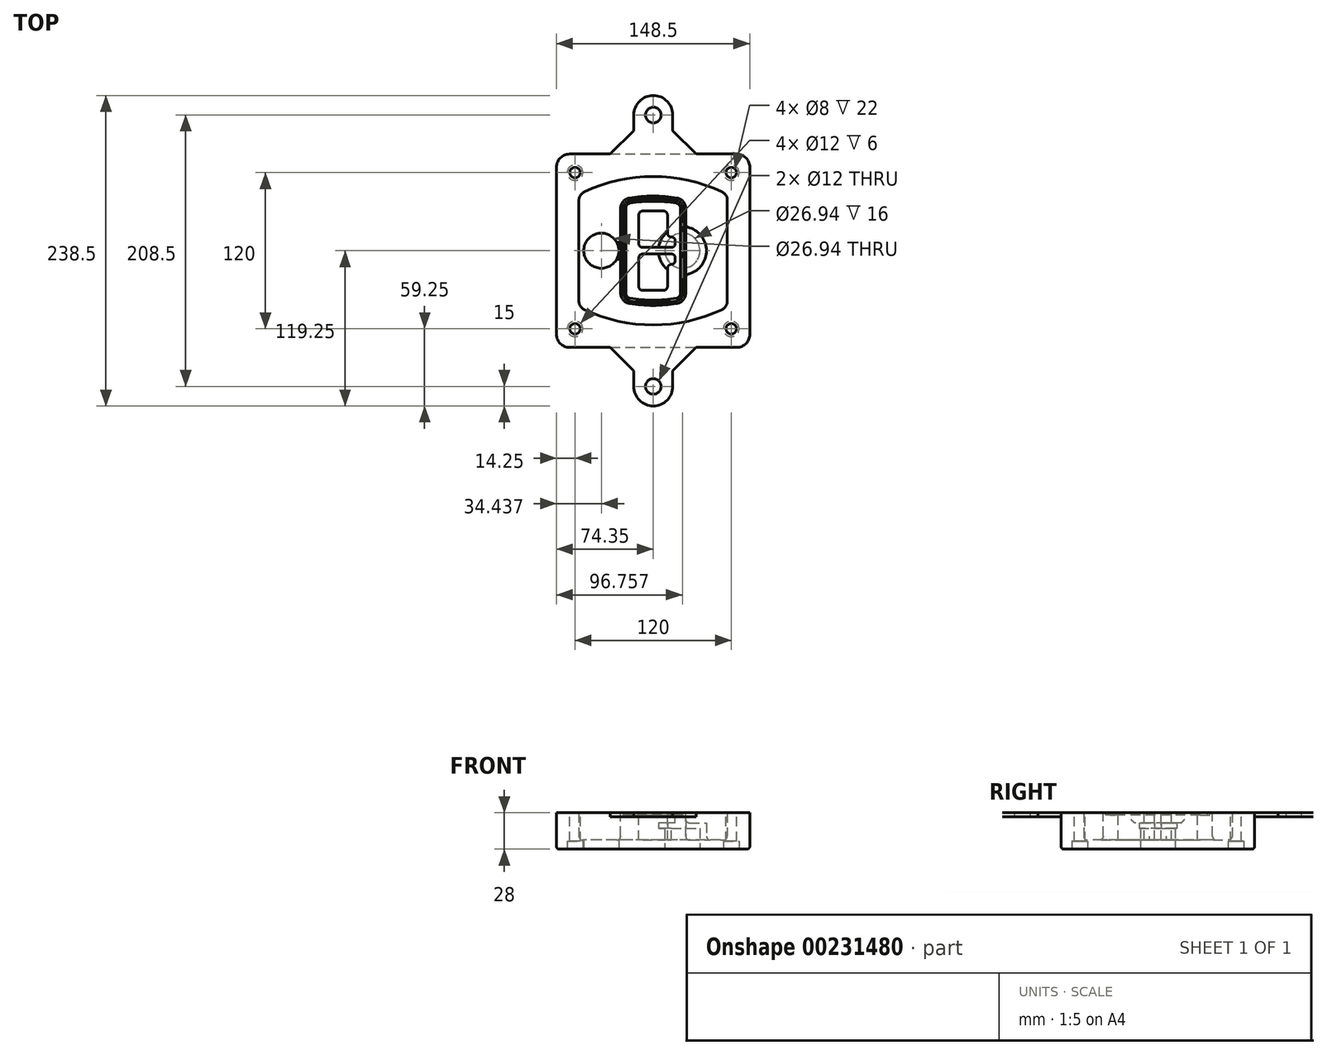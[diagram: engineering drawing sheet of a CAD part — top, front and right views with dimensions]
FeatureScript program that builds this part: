
annotation { "Feature Type Name" : "Feature", "Feature Type Description" : "" }
export const myFeature = defineFeature(function(context is Context, id is Id, definition is map)
    precondition{}
    {
        {
            var Q0;
            Q0=qCreatedBy(makeId("Top.planeOp"),FACE);
            var sketch = newSketch(context, id + "F0", { "sketchPlane" : qUnion([Q0])});
            skPoint(sketch, "E0.rect.middle", {"position": v(0, 0) * mm});
            skLineSegment(sketch, "E1.bottom", {"start": v(-64.25, -74.25) * mm, "end": v(64.25, -74.25) * mm});
            skLineSegment(sketch, "E1.top", {"start": v(-64.25, 74.25) * mm, "end": v(64.25, 74.25) * mm});
            skLineSegment(sketch, "E1.left", {"start": v(-74.25, -64.25) * mm, "end": v(-74.25, 64.25) * mm});
            skLineSegment(sketch, "E1.right", {"start": v(74.25, -64.25) * mm, "end": v(74.25, 64.25) * mm});
            skLineSegment(sketch, "E2", {"start": v(-74.25, 74.25) * mm, "end": v(74.25, -74.25) * mm, "construction": true});
            skLineSegment(sketch, "E3", {"start": v(74.25, 74.25) * mm, "end": v(-74.25, -74.25) * mm, "construction": true});
            skCircle(sketch, "E4", {"center": v(-60, 60) * mm, "radius": 4 * mm});
            skCircle(sketch, "E5", {"center": v(60, 60) * mm, "radius": 4 * mm});
            skCircle(sketch, "E6", {"center": v(60, -60) * mm, "radius": 4 * mm});
            skCircle(sketch, "E7", {"center": v(-60, -60) * mm, "radius": 4 * mm});
            skLineSegment(sketch, "E8", {"start": v(-60, 60) * mm, "end": v(60, 60) * mm, "construction": true});
            skLineSegment(sketch, "E9", {"start": v(60, 60) * mm, "end": v(60, -60) * mm, "construction": true});
            skLineSegment(sketch, "E10", {"start": v(60, -60) * mm, "end": v(-60, -60) * mm, "construction": true});
            skLineSegment(sketch, "E11", {"start": v(-60, -60) * mm, "end": v(-60, 60) * mm, "construction": true});
            skLineSegment(sketch, "E12", {"start": v(-60, 38.83) * mm, "end": v(-60, -38.83) * mm});
            skLineSegment(sketch, "E13", {"start": v(60, 38.83) * mm, "end": v(60, -38.83) * mm});
            skArc(sketch, "E14", {"start": v(54.26, 47.88) * mm, "mid": v(0, 60) * mm, "end": v(-54.26, 47.88) * mm});
            skArc(sketch, "E15", {"start": v(-54.26, -47.88) * mm, "mid": v(0, -60) * mm, "end": v(54.26, -47.88) * mm});
            skLineSegment(sketch, "E16", {"start": v(-60, 0) * mm, "end": v(60, 0) * mm, "construction": true});
            skPoint(sketch, "E17.visualSharp", {"position": v(-60, -45) * mm});
            skArc(sketch, "E17.filletArc", {"start": v(-60, -38.83) * mm, "mid": v(-58.44, -44.2) * mm, "end": v(-54.26, -47.88) * mm});
            skPoint(sketch, "E18.visualSharp", {"position": v(-60, 45) * mm});
            skArc(sketch, "E18.filletArc", {"start": v(-54.26, 47.88) * mm, "mid": v(-58.44, 44.2) * mm, "end": v(-60, 38.83) * mm});
            skPoint(sketch, "E19.visualSharp", {"position": v(60, 45) * mm});
            skArc(sketch, "E19.filletArc", {"start": v(60, 38.83) * mm, "mid": v(58.44, 44.2) * mm, "end": v(54.26, 47.88) * mm});
            skPoint(sketch, "E20.visualSharp", {"position": v(60, -45) * mm});
            skArc(sketch, "E20.filletArc", {"start": v(54.26, -47.88) * mm, "mid": v(58.44, -44.2) * mm, "end": v(60, -38.83) * mm});
            skPoint(sketch, "E21.visualSharp", {"position": v(-74.25, 74.25) * mm});
            skArc(sketch, "E21.filletArc", {"start": v(-64.25, 74.25) * mm, "mid": v(-71.32, 71.32) * mm, "end": v(-74.25, 64.25) * mm});
            skPoint(sketch, "E22.visualSharp", {"position": v(74.25, 74.25) * mm});
            skArc(sketch, "E22.filletArc", {"start": v(74.25, 64.25) * mm, "mid": v(71.32, 71.32) * mm, "end": v(64.25, 74.25) * mm});
            skPoint(sketch, "E23.visualSharp", {"position": v(74.25, -74.25) * mm});
            skArc(sketch, "E23.filletArc", {"start": v(64.25, -74.25) * mm, "mid": v(71.32, -71.32) * mm, "end": v(74.25, -64.25) * mm});
            skPoint(sketch, "E24.visualSharp", {"position": v(-74.25, -74.25) * mm});
            skArc(sketch, "E24.filletArc", {"start": v(-74.25, -64.25) * mm, "mid": v(-71.32, -71.32) * mm, "end": v(-64.25, -74.25) * mm});
            skArc(sketch, "E25.0", {"start": v(57, 38.83) * mm, "mid": v(55.9, 42.58) * mm, "end": v(52.98, 45.17) * mm});
            skLineSegment(sketch, "E25.1", {"start": v(57, 38.83) * mm, "end": v(57, -38.83) * mm});
            skArc(sketch, "E25.2", {"start": v(52.98, -45.17) * mm, "mid": v(55.9, -42.58) * mm, "end": v(57, -38.83) * mm});
            skArc(sketch, "E25.3", {"start": v(-52.98, -45.17) * mm, "mid": v(0, -57) * mm, "end": v(52.98, -45.17) * mm});
            skArc(sketch, "E25.4", {"start": v(-57, -38.83) * mm, "mid": v(-55.9, -42.58) * mm, "end": v(-52.98, -45.17) * mm});
            skArc(sketch, "E25.5", {"start": v(52.98, 45.17) * mm, "mid": v(0, 57) * mm, "end": v(-52.98, 45.17) * mm});
            skLineSegment(sketch, "E25.6", {"start": v(-57, 38.83) * mm, "end": v(-57, -38.83) * mm});
            skArc(sketch, "E25.7", {"start": v(-52.98, 45.17) * mm, "mid": v(-55.9, 42.58) * mm, "end": v(-57, 38.83) * mm});
            skArc(sketch, "E26.0", {"start": v(-55.96, 51.5) * mm, "mid": v(-61.82, 46.33) * mm, "end": v(-64, 38.83) * mm});
            skArc(sketch, "E26.1", {"start": v(55.96, 51.5) * mm, "mid": v(0, 64) * mm, "end": v(-55.96, 51.5) * mm});
            skArc(sketch, "E26.2", {"start": v(64, 38.83) * mm, "mid": v(61.82, 46.33) * mm, "end": v(55.96, 51.5) * mm});
            skLineSegment(sketch, "E26.3", {"start": v(64, 38.83) * mm, "end": v(64, -38.83) * mm});
            skArc(sketch, "E26.4", {"start": v(55.96, -51.5) * mm, "mid": v(61.82, -46.33) * mm, "end": v(64, -38.83) * mm});
            skLineSegment(sketch, "E26.5", {"start": v(-64, 38.83) * mm, "end": v(-64, -38.83) * mm});
            skArc(sketch, "E26.6", {"start": v(-55.96, -51.5) * mm, "mid": v(0, -64) * mm, "end": v(55.96, -51.5) * mm});
            skArc(sketch, "E26.7", {"start": v(-64, -38.83) * mm, "mid": v(-61.82, -46.33) * mm, "end": v(-55.96, -51.5) * mm});
            skSolve(sketch);
        }
        {
            var Q0;
            Q0=makeQuery(id+"F0.imprint","IMPRINT",FACE,{"disambiguationData":[TD([[makeQuery(id+"F0.imprint","IMPRINT",EDGE,{"derivedFrom":sQuery(id+"F0.wireOp",EDGE,"E1.bottom")}),1.0]])]});
            var Q1;
            Q1=makeQuery(id+"F0.imprint","IMPRINT",FACE,{"disambiguationData":[TD([[makeQuery(id+"F0.imprint","IMPRINT",EDGE,{"derivedFrom":sQuery(id+"F0.wireOp",EDGE,"E12")}),1.0]])]});
            var Q2;
            Q2=makeQuery(id+"F0.imprint","IMPRINT",FACE,{"disambiguationData":[TD([[makeQuery(id+"F0.imprint","IMPRINT",EDGE,{"derivedFrom":sQuery(id+"F0.wireOp",EDGE,"E25.0")}),1.0]])]});
            var Q3;
            Q3=makeQuery(id+"F0.imprint","IMPRINT",FACE,{"disambiguationData":[TD([[makeQuery(id+"F0.imprint","IMPRINT",EDGE,{"derivedFrom":sQuery(id+"F0.wireOp",EDGE,"E12")}),-1.0]])]});
            extrude(context, id + "F1", {"entities" : qUnion([Q0, Q1, Q2, Q3]), "oppositeDirection" : true, "depth" : 25 * mm});
        }
        {
            var Q0;
            Q0=makeQuery(id+"F0.imprint","IMPRINT",FACE,{"disambiguationData":[TD([[makeQuery(id+"F0.imprint","IMPRINT",EDGE,{"derivedFrom":sQuery(id+"F0.wireOp",EDGE,"E12")}),1.0]])]});
            extrude(context, id + "F2", {"entities" : qUnion([Q0]), "operationType" : NewBodyOperationType.ADD, "depth" : 3 * mm});
        }
        {
            var Q0;
            Q0=makeQuery(id+"F0.imprint","IMPRINT",FACE,{"disambiguationData":[TD([[makeQuery(id+"F0.imprint","IMPRINT",EDGE,{"derivedFrom":sQuery(id+"F0.wireOp",EDGE,"E25.0")}),1.0]])]});
            extrude(context, id + "F3", {"entities" : qUnion([Q0]), "operationType" : NewBodyOperationType.REMOVE, "oppositeDirection" : true, "depth" : 18 * mm});
        }
        {
            var Q0;
            Q0=makeQuery(id+"F2.opExtrude","CAP_FACE",FACE,{"disambiguationData":[OSD([sQuery(id+"F0.wireOp",EDGE,"E12"),sQuery(id+"F0.wireOp",EDGE,"E13"),sQuery(id+"F0.wireOp",EDGE,"E14"),sQuery(id+"F0.wireOp",EDGE,"E15"),sQuery(id+"F0.wireOp",EDGE,"E17.filletArc"),sQuery(id+"F0.wireOp",EDGE,"E18.filletArc"),sQuery(id+"F0.wireOp",EDGE,"E19.filletArc"),sQuery(id+"F0.wireOp",EDGE,"E20.filletArc"),sQuery(id+"F0.wireOp",EDGE,"E25.0"),sQuery(id+"F0.wireOp",EDGE,"E25.1"),sQuery(id+"F0.wireOp",EDGE,"E25.2"),sQuery(id+"F0.wireOp",EDGE,"E25.3"),sQuery(id+"F0.wireOp",EDGE,"E25.4"),sQuery(id+"F0.wireOp",EDGE,"E25.5"),sQuery(id+"F0.wireOp",EDGE,"E25.6"),sQuery(id+"F0.wireOp",EDGE,"E25.7")])],"isStart":false});
            var sketch = newSketch(context, id + "F4", { "sketchPlane" : qUnion([Q0])});
            skArc(sketch, "E27.0", {"start": v(-18.34, -40.45) * mm, "mid": v(0, -42) * mm, "end": v(18.34, -40.45) * mm});
            skArc(sketch, "E28.0", {"start": v(18.34, 40.45) * mm, "mid": v(0, 42) * mm, "end": v(-18.34, 40.45) * mm});
            skLineSegment(sketch, "E29", {"start": v(-25, 32.57) * mm, "end": v(-25, -32.57) * mm});
            skLineSegment(sketch, "E30", {"start": v(25, 32.57) * mm, "end": v(25, -32.57) * mm});
            skLineSegment(sketch, "E31", {"start": v(-25, 39.1) * mm, "end": v(25, 39.1) * mm, "construction": true});
            skLineSegment(sketch, "E32", {"start": v(-25, -39.1) * mm, "end": v(25, -39.1) * mm, "construction": true});
            skPoint(sketch, "E33.visualSharp", {"position": v(-25, 39.1) * mm});
            skArc(sketch, "E33.filletArc", {"start": v(-18.34, 40.45) * mm, "mid": v(-23.11, 37.73) * mm, "end": v(-25, 32.57) * mm});
            skPoint(sketch, "E34.visualSharp", {"position": v(25, 39.1) * mm});
            skArc(sketch, "E34.filletArc", {"start": v(25, 32.57) * mm, "mid": v(23.11, 37.73) * mm, "end": v(18.34, 40.45) * mm});
            skPoint(sketch, "E35.visualSharp", {"position": v(25, -39.1) * mm});
            skArc(sketch, "E35.filletArc", {"start": v(18.34, -40.45) * mm, "mid": v(23.11, -37.73) * mm, "end": v(25, -32.57) * mm});
            skPoint(sketch, "E36.visualSharp", {"position": v(-25, -39.1) * mm});
            skArc(sketch, "E36.filletArc", {"start": v(-25, -32.57) * mm, "mid": v(-23.11, -37.73) * mm, "end": v(-18.34, -40.45) * mm});
            skArc(sketch, "E37.0", {"start": v(52.98, 45.17) * mm, "mid": v(0, 57) * mm, "end": v(-52.98, 45.17) * mm});
            skArc(sketch, "E37.1", {"start": v(-52.98, 45.17) * mm, "mid": v(-55.9, 42.58) * mm, "end": v(-57, 38.83) * mm});
            skLineSegment(sketch, "E37.2", {"start": v(-57, 38.83) * mm, "end": v(-57, -38.83) * mm});
            skArc(sketch, "E37.3", {"start": v(-57, -38.83) * mm, "mid": v(-55.9, -42.58) * mm, "end": v(-52.98, -45.17) * mm});
            skArc(sketch, "E37.4", {"start": v(-52.98, -45.17) * mm, "mid": v(0, -57) * mm, "end": v(52.98, -45.17) * mm});
            skArc(sketch, "E37.5", {"start": v(52.98, -45.17) * mm, "mid": v(55.9, -42.58) * mm, "end": v(57, -38.83) * mm});
            skLineSegment(sketch, "E37.6", {"start": v(57, 38.83) * mm, "end": v(57, -38.83) * mm});
            skArc(sketch, "E37.7", {"start": v(57, 38.83) * mm, "mid": v(55.9, 42.58) * mm, "end": v(52.98, 45.17) * mm});
            skLineSegment(sketch, "E38.0", {"start": v(23, 32.57) * mm, "end": v(23, -32.57) * mm});
            skArc(sketch, "E38.1", {"start": v(18, -38.48) * mm, "mid": v(21.58, -36.44) * mm, "end": v(23, -32.57) * mm});
            skArc(sketch, "E38.2", {"start": v(-18, -38.48) * mm, "mid": v(0, -40) * mm, "end": v(18, -38.48) * mm});
            skArc(sketch, "E38.3", {"start": v(-23, -32.57) * mm, "mid": v(-21.58, -36.44) * mm, "end": v(-18, -38.48) * mm});
            skLineSegment(sketch, "E38.4", {"start": v(-23, 32.57) * mm, "end": v(-23, -32.57) * mm});
            skArc(sketch, "E38.5", {"start": v(23, 32.57) * mm, "mid": v(21.58, 36.44) * mm, "end": v(18, 38.48) * mm});
            skArc(sketch, "E38.6", {"start": v(-18, 38.48) * mm, "mid": v(-21.58, 36.44) * mm, "end": v(-23, 32.57) * mm});
            skArc(sketch, "E38.7", {"start": v(18, 38.48) * mm, "mid": v(0, 40) * mm, "end": v(-18, 38.48) * mm});
            skArc(sketch, "E39.0", {"start": v(21, 32.57) * mm, "mid": v(20.06, 35.15) * mm, "end": v(17.67, 36.5) * mm});
            skLineSegment(sketch, "E39.1", {"start": v(21, 32.57) * mm, "end": v(21, -32.57) * mm});
            skArc(sketch, "E39.2", {"start": v(17.67, -36.5) * mm, "mid": v(20.06, -35.15) * mm, "end": v(21, -32.57) * mm});
            skArc(sketch, "E39.3", {"start": v(-17.67, -36.5) * mm, "mid": v(0, -38) * mm, "end": v(17.67, -36.5) * mm});
            skArc(sketch, "E39.4", {"start": v(-21, -32.57) * mm, "mid": v(-20.06, -35.15) * mm, "end": v(-17.67, -36.5) * mm});
            skArc(sketch, "E39.5", {"start": v(17.67, 36.5) * mm, "mid": v(0, 38) * mm, "end": v(-17.67, 36.5) * mm});
            skLineSegment(sketch, "E39.6", {"start": v(-21, 32.57) * mm, "end": v(-21, -32.57) * mm});
            skArc(sketch, "E39.7", {"start": v(-17.67, 36.5) * mm, "mid": v(-20.06, 35.15) * mm, "end": v(-21, 32.57) * mm});
            skLineSegment(sketch, "E40", {"start": v(-25, 0) * mm, "end": v(25, 0) * mm, "construction": true});
            skLineSegment(sketch, "E41", {"start": v(-11, 5.5) * mm, "end": v(-11, 27.5) * mm});
            skLineSegment(sketch, "E42", {"start": v(-8, 30.5) * mm, "end": v(8, 30.5) * mm});
            skLineSegment(sketch, "E43", {"start": v(11, 27.5) * mm, "end": v(11, 13.5) * mm});
            skLineSegment(sketch, "E44", {"start": v(14, 10.5) * mm, "end": v(14, 10.5) * mm});
            skLineSegment(sketch, "E45", {"start": v(17, 7.5) * mm, "end": v(17, 5.5) * mm});
            skLineSegment(sketch, "E46", {"start": v(14, 2.5) * mm, "end": v(-8, 2.5) * mm});
            skPoint(sketch, "E47.visualSharp", {"position": v(-11, 30.5) * mm});
            skArc(sketch, "E47.filletArc", {"start": v(-8, 30.5) * mm, "mid": v(-10.12, 29.62) * mm, "end": v(-11, 27.5) * mm});
            skPoint(sketch, "E48.visualSharp", {"position": v(11, 30.5) * mm});
            skArc(sketch, "E48.filletArc", {"start": v(11, 27.5) * mm, "mid": v(10.12, 29.62) * mm, "end": v(8, 30.5) * mm});
            skPoint(sketch, "E49.visualSharp", {"position": v(11, 10.5) * mm});
            skArc(sketch, "E49.filletArc", {"start": v(11, 13.5) * mm, "mid": v(11.88, 11.38) * mm, "end": v(14, 10.5) * mm});
            skPoint(sketch, "E50.visualSharp", {"position": v(17, 10.5) * mm});
            skArc(sketch, "E50.filletArc", {"start": v(17, 7.5) * mm, "mid": v(16.12, 9.62) * mm, "end": v(14, 10.5) * mm});
            skPoint(sketch, "E51.visualSharp", {"position": v(17, 2.5) * mm});
            skArc(sketch, "E51.filletArc", {"start": v(14, 2.5) * mm, "mid": v(16.12, 3.38) * mm, "end": v(17, 5.5) * mm});
            skPoint(sketch, "E52.visualSharp", {"position": v(-11, 2.5) * mm});
            skArc(sketch, "E52.filletArc", {"start": v(-11, 5.5) * mm, "mid": v(-10.12, 3.38) * mm, "end": v(-8, 2.5) * mm});
            skLineSegment(sketch, "E53.0.MirrorCS", {"start": v(14, -2.5) * mm, "end": v(-8, -2.5) * mm});
            skArc(sketch, "E54.0.MirrorCS", {"start": v(-11, -5.5) * mm, "mid": v(-10.12, -3.38) * mm, "end": v(-8, -2.5) * mm});
            skLineSegment(sketch, "E55.0.MirrorCS", {"start": v(-11, -5.5) * mm, "end": v(-11, -27.5) * mm});
            skArc(sketch, "E56.0.MirrorCS", {"start": v(-8, -30.5) * mm, "mid": v(-10.12, -29.62) * mm, "end": v(-11, -27.5) * mm});
            skLineSegment(sketch, "E57.0.MirrorCS", {"start": v(-8, -30.5) * mm, "end": v(8, -30.5) * mm});
            skArc(sketch, "E58.0.MirrorCS", {"start": v(11, -27.5) * mm, "mid": v(10.12, -29.62) * mm, "end": v(8, -30.5) * mm});
            skLineSegment(sketch, "E59.0.MirrorCS", {"start": v(11, -27.5) * mm, "end": v(11, -13.5) * mm});
            skArc(sketch, "E60.0.MirrorCS", {"start": v(11, -13.5) * mm, "mid": v(11.88, -11.38) * mm, "end": v(14, -10.5) * mm});
            skArc(sketch, "E61.0.MirrorCS", {"start": v(17, -7.5) * mm, "mid": v(16.12, -9.62) * mm, "end": v(14, -10.5) * mm});
            skLineSegment(sketch, "E62.0.MirrorCS", {"start": v(17, -7.5) * mm, "end": v(17, -5.5) * mm});
            skArc(sketch, "E63.0.MirrorCS", {"start": v(14, -2.5) * mm, "mid": v(16.12, -3.38) * mm, "end": v(17, -5.5) * mm});
            skSolve(sketch);
        }
        {
            var Q0;
            Q0=makeQuery(id+"F4.imprint","IMPRINT",FACE,{"disambiguationData":[TD([[makeQuery(id+"F4.imprint","IMPRINT",EDGE,{"derivedFrom":sQuery(id+"F4.wireOp",EDGE,"E27.0")}),1.0]])]});
            var Q1;
            Q1=makeQuery(id+"F4.imprint","IMPRINT",FACE,{"disambiguationData":[TD([[makeQuery(id+"F4.imprint","IMPRINT",EDGE,{"derivedFrom":sQuery(id+"F4.wireOp",EDGE,"E38.0")}),-1.0]])]});
            var Q2;
            Q2=makeQuery(id+"F4.imprint","IMPRINT",FACE,{"disambiguationData":[TD([[makeQuery(id+"F4.imprint","IMPRINT",EDGE,{"derivedFrom":sQuery(id+"F4.wireOp",EDGE,"E39.0")}),1.0]])]});
            extrude(context, id + "F5", {"entities" : qUnion([Q0, Q1, Q2]), "operationType" : NewBodyOperationType.ADD, "endBound" : BoundingType.UP_TO_NEXT, "oppositeDirection" : true, "depth" : 25 * mm});
        }
        {
            var Q0;
            Q0=makeQuery(id+"F4.imprint","IMPRINT",FACE,{"disambiguationData":[TD([[makeQuery(id+"F4.imprint","IMPRINT",EDGE,{"derivedFrom":sQuery(id+"F4.wireOp",EDGE,"E38.0")}),-1.0]])]});
            extrude(context, id + "F6", {"entities" : qUnion([Q0]), "operationType" : NewBodyOperationType.REMOVE, "oppositeDirection" : true, "depth" : 2 * mm});
        }
        {
            var Q0;
            Q0=makeQuery(id+"F1.opExtrude","CAP_FACE",FACE,{"disambiguationData":[OSD([sQuery(id+"F0.wireOp",EDGE,"E1.bottom"),sQuery(id+"F0.wireOp",EDGE,"E1.top"),sQuery(id+"F0.wireOp",EDGE,"E1.left"),sQuery(id+"F0.wireOp",EDGE,"E1.right"),sQuery(id+"F0.wireOp",EDGE,"E4"),sQuery(id+"F0.wireOp",EDGE,"E5"),sQuery(id+"F0.wireOp",EDGE,"E6"),sQuery(id+"F0.wireOp",EDGE,"E7"),sQuery(id+"F0.wireOp",EDGE,"E21.filletArc"),sQuery(id+"F0.wireOp",EDGE,"E22.filletArc"),sQuery(id+"F0.wireOp",EDGE,"E23.filletArc"),sQuery(id+"F0.wireOp",EDGE,"E24.filletArc")])],"isStart":false});
            var sketch = newSketch(context, id + "F7", { "sketchPlane" : qUnion([Q0])});
            skCircle(sketch, "E64", {"center": v(22.5, 0) * mm, "radius": 13.47 * mm});
            skCircle(sketch, "E65", {"center": v(-39.81, 0) * mm, "radius": 13.47 * mm});
            skLineSegment(sketch, "E66", {"start": v(74.25, 0) * mm, "end": v(-74.25, 0) * mm});
            skCircle(sketch, "E67", {"center": v(22.5, 0) * mm, "radius": 18.47 * mm});
            skCircle(sketch, "E68", {"center": v(60, -60) * mm, "radius": 6 * mm});
            skCircle(sketch, "E69", {"center": v(-60, -60) * mm, "radius": 6 * mm});
            skCircle(sketch, "E70", {"center": v(-60, 60) * mm, "radius": 6 * mm});
            skCircle(sketch, "E71", {"center": v(60, 60) * mm, "radius": 6 * mm});
            skSolve(sketch);
        }
        {
            var Q0;
            {var subQ1=sQuery(id+"F7.wireOp",EDGE,"E66");var subQ4=sQuery(id+"F7.wireOp",EDGE,"E64");var subQ6=makeQuery(id+"F7.imprint","INTERSECT",VERTEX,{"disambiguationData":[OD(0.0)],"derivedFrom":[subQ4,subQ1]});Q0=makeQuery(id+"F7.imprint","IMPRINT",FACE,{"disambiguationData":[TD([[makeQuery(id+"F7.imprint","IMPRINT",EDGE,{"disambiguationData":[TD([[subQ6,-1.0]])],"derivedFrom":subQ4}),-1.0]])]});}
            var Q1;
            {var subQ0=sQuery(id+"F7.wireOp",EDGE,"E66");var subQ1=sQuery(id+"F7.wireOp",EDGE,"E64");var subQ3=makeQuery(id+"F7.imprint","INTERSECT",VERTEX,{"disambiguationData":[OD(0.0)],"derivedFrom":[subQ1,subQ0]});Q1=makeQuery(id+"F7.imprint","IMPRINT",FACE,{"disambiguationData":[TD([[makeQuery(id+"F7.imprint","IMPRINT",EDGE,{"disambiguationData":[TD([[subQ3,-1.0]])],"derivedFrom":subQ1}),1.0]])]});}
            var Q2;
            {var subQ0=sQuery(id+"F7.wireOp",EDGE,"E66");var subQ1=sQuery(id+"F7.wireOp",EDGE,"E64");var subQ3=makeQuery(id+"F7.imprint","INTERSECT",VERTEX,{"disambiguationData":[OD(0.0)],"derivedFrom":[subQ1,subQ0]});Q2=makeQuery(id+"F7.imprint","IMPRINT",FACE,{"disambiguationData":[TD([[makeQuery(id+"F7.imprint","IMPRINT",EDGE,{"disambiguationData":[TD([[subQ3,1.0]])],"derivedFrom":subQ1}),1.0]])]});}
            var Q3;
            {var subQ1=sQuery(id+"F7.wireOp",EDGE,"E66");var subQ4=sQuery(id+"F7.wireOp",EDGE,"E64");var subQ6=makeQuery(id+"F7.imprint","INTERSECT",VERTEX,{"disambiguationData":[OD(0.0)],"derivedFrom":[subQ4,subQ1]});Q3=makeQuery(id+"F7.imprint","IMPRINT",FACE,{"disambiguationData":[TD([[makeQuery(id+"F7.imprint","IMPRINT",EDGE,{"disambiguationData":[TD([[subQ6,1.0]])],"derivedFrom":subQ4}),-1.0]])]});}
            extrude(context, id + "F8", {"entities" : qUnion([Q0, Q1, Q2, Q3]), "operationType" : NewBodyOperationType.ADD, "oppositeDirection" : true, "depth" : 20 * mm});
        }
        {
            var Q0;
            {var subQ0=sQuery(id+"F7.wireOp",EDGE,"E66");var subQ1=sQuery(id+"F7.wireOp",EDGE,"E64");var subQ3=makeQuery(id+"F7.imprint","INTERSECT",VERTEX,{"disambiguationData":[OD(0.0)],"derivedFrom":[subQ1,subQ0]});Q0=makeQuery(id+"F7.imprint","IMPRINT",FACE,{"disambiguationData":[TD([[makeQuery(id+"F7.imprint","IMPRINT",EDGE,{"disambiguationData":[TD([[subQ3,-1.0]])],"derivedFrom":subQ1}),1.0]])]});}
            var Q1;
            {var subQ0=sQuery(id+"F7.wireOp",EDGE,"E66");var subQ1=sQuery(id+"F7.wireOp",EDGE,"E64");var subQ3=makeQuery(id+"F7.imprint","INTERSECT",VERTEX,{"disambiguationData":[OD(0.0)],"derivedFrom":[subQ1,subQ0]});Q1=makeQuery(id+"F7.imprint","IMPRINT",FACE,{"disambiguationData":[TD([[makeQuery(id+"F7.imprint","IMPRINT",EDGE,{"disambiguationData":[TD([[subQ3,1.0]])],"derivedFrom":subQ1}),1.0]])]});}
            extrude(context, id + "F9", {"entities" : qUnion([Q0, Q1]), "operationType" : NewBodyOperationType.REMOVE, "oppositeDirection" : true, "depth" : 16 * mm});
        }
        {
            var Q0;
            {var subQ0=sQuery(id+"F7.wireOp",EDGE,"E66");var subQ1=sQuery(id+"F7.wireOp",EDGE,"E65");var subQ3=makeQuery(id+"F7.imprint","INTERSECT",VERTEX,{"disambiguationData":[OD(0.0)],"derivedFrom":[subQ1,subQ0]});Q0=makeQuery(id+"F7.imprint","IMPRINT",FACE,{"disambiguationData":[TD([[makeQuery(id+"F7.imprint","IMPRINT",EDGE,{"disambiguationData":[TD([[subQ3,-1.0]])],"derivedFrom":subQ1}),1.0]])]});}
            var Q1;
            {var subQ0=sQuery(id+"F7.wireOp",EDGE,"E66");var subQ1=sQuery(id+"F7.wireOp",EDGE,"E65");var subQ3=makeQuery(id+"F7.imprint","INTERSECT",VERTEX,{"disambiguationData":[OD(0.0)],"derivedFrom":[subQ1,subQ0]});Q1=makeQuery(id+"F7.imprint","IMPRINT",FACE,{"disambiguationData":[TD([[makeQuery(id+"F7.imprint","IMPRINT",EDGE,{"disambiguationData":[TD([[subQ3,1.0]])],"derivedFrom":subQ1}),1.0]])]});}
            extrude(context, id + "F10", {"entities" : qUnion([Q0, Q1]), "operationType" : NewBodyOperationType.REMOVE, "oppositeDirection" : true, "depth" : 25 * mm});
        }
        {
            var Q0;
            Q0=makeQuery(id+"F7.imprint","IMPRINT",FACE,{"disambiguationData":[TD([[makeQuery(id+"F7.imprint","IMPRINT",EDGE,{"derivedFrom":sQuery(id+"F7.wireOp",EDGE,"E68")}),1.0]])]});
            var Q1;
            Q1=makeQuery(id+"F7.imprint","IMPRINT",FACE,{"disambiguationData":[TD([[makeQuery(id+"F7.imprint","IMPRINT",EDGE,{"derivedFrom":makeQuery(id+"F1.opExtrude","CAP_EDGE",EDGE,{"disambiguationData":[OSD([sQuery(id+"F0.wireOp",EDGE,"E5")])],"isStart":false})}),-1.0]])]});
            var Q2;
            Q2=makeQuery(id+"F7.imprint","IMPRINT",FACE,{"disambiguationData":[TD([[makeQuery(id+"F7.imprint","IMPRINT",EDGE,{"derivedFrom":sQuery(id+"F7.wireOp",EDGE,"E69")}),1.0]])]});
            var Q3;
            Q3=makeQuery(id+"F7.imprint","IMPRINT",FACE,{"disambiguationData":[TD([[makeQuery(id+"F7.imprint","IMPRINT",EDGE,{"derivedFrom":makeQuery(id+"F1.opExtrude","CAP_EDGE",EDGE,{"disambiguationData":[OSD([sQuery(id+"F0.wireOp",EDGE,"E4")])],"isStart":false})}),-1.0]])]});
            var Q4;
            Q4=makeQuery(id+"F7.imprint","IMPRINT",FACE,{"disambiguationData":[TD([[makeQuery(id+"F7.imprint","IMPRINT",EDGE,{"derivedFrom":sQuery(id+"F7.wireOp",EDGE,"E70")}),1.0]])]});
            var Q5;
            Q5=makeQuery(id+"F7.imprint","IMPRINT",FACE,{"disambiguationData":[TD([[makeQuery(id+"F7.imprint","IMPRINT",EDGE,{"derivedFrom":makeQuery(id+"F1.opExtrude","CAP_EDGE",EDGE,{"disambiguationData":[OSD([sQuery(id+"F0.wireOp",EDGE,"E7")])],"isStart":false})}),-1.0]])]});
            var Q6;
            Q6=makeQuery(id+"F7.imprint","IMPRINT",FACE,{"disambiguationData":[TD([[makeQuery(id+"F7.imprint","IMPRINT",EDGE,{"derivedFrom":sQuery(id+"F7.wireOp",EDGE,"E71")}),1.0]])]});
            var Q7;
            Q7=makeQuery(id+"F7.imprint","IMPRINT",FACE,{"disambiguationData":[TD([[makeQuery(id+"F7.imprint","IMPRINT",EDGE,{"derivedFrom":makeQuery(id+"F1.opExtrude","CAP_EDGE",EDGE,{"disambiguationData":[OSD([sQuery(id+"F0.wireOp",EDGE,"E6")])],"isStart":false})}),-1.0]])]});
            extrude(context, id + "F11", {"entities" : qUnion([Q0, Q1, Q2, Q3, Q4, Q5, Q6, Q7]), "operationType" : NewBodyOperationType.REMOVE, "oppositeDirection" : true, "depth" : 6 * mm});
        }
        {
            var Q0;
            Q0=makeQuery(id+"F9.boolean.opBoolean","COPY",FACE,{"derivedFrom":makeQuery(id+"F9.opExtrude","CAP_FACE",FACE,{"disambiguationData":[OSD([sQuery(id+"F7.wireOp",EDGE,"E64")])],"isStart":false})});
            var sketch = newSketch(context, id + "F12", { "sketchPlane" : qUnion([Q0])});
            skArc(sketch, "E72.0", {"start": v(11, 14.45) * mm, "mid": v(6.45, 9.13) * mm, "end": v(4.2, 2.5) * mm});
            skArc(sketch, "E72.1", {"start": v(4.2, -2.5) * mm, "mid": v(6.45, -9.13) * mm, "end": v(11, -14.45) * mm});
            skLineSegment(sketch, "E73", {"start": v(4.2, -2.5) * mm, "end": v(14, -2.5) * mm});
            skLineSegment(sketch, "E74.0", {"start": v(14, 2.5) * mm, "end": v(4.2, 2.5) * mm});
            skArc(sketch, "E74.1", {"start": v(14, 2.5) * mm, "mid": v(16.12, 3.38) * mm, "end": v(17, 5.5) * mm});
            skLineSegment(sketch, "E74.2", {"start": v(17, 7.5) * mm, "end": v(17, 5.5) * mm});
            skArc(sketch, "E74.3", {"start": v(17, 7.5) * mm, "mid": v(16.12, 9.62) * mm, "end": v(14, 10.5) * mm});
            skArc(sketch, "E74.4", {"start": v(11, 13.5) * mm, "mid": v(11.88, 11.38) * mm, "end": v(14, 10.5) * mm});
            skLineSegment(sketch, "E74.5", {"start": v(11, 14.45) * mm, "end": v(11, 13.5) * mm});
            skLineSegment(sketch, "E74.7", {"start": v(14, -2.5) * mm, "end": v(4.2, -2.5) * mm});
            skArc(sketch, "E74.8", {"start": v(14, -2.5) * mm, "mid": v(16.12, -3.38) * mm, "end": v(17, -5.5) * mm});
            skLineSegment(sketch, "E74.9", {"start": v(17, -7.5) * mm, "end": v(17, -5.5) * mm});
            skArc(sketch, "E74.10", {"start": v(17, -7.5) * mm, "mid": v(16.12, -9.62) * mm, "end": v(14, -10.5) * mm});
            skArc(sketch, "E74.11", {"start": v(11, -13.5) * mm, "mid": v(11.88, -11.38) * mm, "end": v(14, -10.5) * mm});
            skLineSegment(sketch, "E74.12", {"start": v(11, -14.45) * mm, "end": v(11, -13.5) * mm});
            skPoint(sketch, "E75.orphan", {"position": v(11, -27.5) * mm});
            skPoint(sketch, "E76.orphan", {"position": v(-8, -2.5) * mm});
            skPoint(sketch, "E77.orphan", {"position": v(-8, 2.5) * mm});
            skPoint(sketch, "E78.orphan", {"position": v(11, 27.5) * mm});
            skSolve(sketch);
        }
        {
            var Q0;
            {var subQ7=sQuery(id+"F12.wireOp",EDGE,"E72.0");var subQ14=sQuery(id+"F12.wireOp",EDGE,"E72.1");var subQ16=sQuery(id+"F12.wireOp",EDGE,"E74.1");var subQ18=sQuery(id+"F12.wireOp",EDGE,"E74.8");Q0=qUnion([makeQuery(id+"F12.imprint","IMPRINT",FACE,{"disambiguationData":[TD([[makeQuery(id+"F12.imprint","IMPRINT",EDGE,{"derivedFrom":subQ7}),1.0]])]}),makeQuery(id+"F12.imprint","IMPRINT",FACE,{"disambiguationData":[TD([[makeQuery(id+"F12.imprint","IMPRINT",EDGE,{"derivedFrom":subQ14}),1.0]])]}),makeQuery(id+"F12.imprint","IMPRINT",FACE,{"disambiguationData":[TD([[makeQuery(id+"F12.imprint","IMPRINT",EDGE,{"derivedFrom":subQ16}),1.0]])]}),makeQuery(id+"F12.imprint","IMPRINT",FACE,{"disambiguationData":[TD([[makeQuery(id+"F12.imprint","IMPRINT",EDGE,{"derivedFrom":subQ18}),-1.0]])]})]);}
            var Q1;
            Q1=makeQuery(id+"F5.boolean.opBoolean","SPLIT",FACE,{"disambiguationData":[TD([makeQuery(id+"F5.opExtrude","SWEPT_FACE",FACE,{"disambiguationData":[OSD([sQuery(id+"F4.wireOp",EDGE,"E41")])]})])],"derivedFrom":makeQuery(id+"F3.boolean.opBoolean","COPY",FACE,{"derivedFrom":makeQuery(id+"F3.opExtrude","CAP_FACE",FACE,{"disambiguationData":[OSD([sQuery(id+"F0.wireOp",EDGE,"E25.0"),sQuery(id+"F0.wireOp",EDGE,"E25.1"),sQuery(id+"F0.wireOp",EDGE,"E25.2"),sQuery(id+"F0.wireOp",EDGE,"E25.3"),sQuery(id+"F0.wireOp",EDGE,"E25.4"),sQuery(id+"F0.wireOp",EDGE,"E25.5"),sQuery(id+"F0.wireOp",EDGE,"E25.6"),sQuery(id+"F0.wireOp",EDGE,"E25.7")])],"isStart":false})})});
            extrude(context, id + "F13", {"entities" : qUnion([Q0]), "operationType" : NewBodyOperationType.REMOVE, "endBound" : BoundingType.UP_TO_SURFACE, "endBoundEntityFace" : qUnion([Q1]), "depth" : 25 * mm});
        }
        {
            var Q0;
            Q0=makeQuery(id+"F3.boolean.opBoolean","COPY",EDGE,{"derivedFrom":makeQuery(id+"F3.opExtrude","CAP_EDGE",EDGE,{"disambiguationData":[OSD([sQuery(id+"F0.wireOp",EDGE,"E25.6")])],"isStart":false})});
            var Q1;
            Q1=makeQuery(id+"F8.boolean.opBoolean","INTERSECT",EDGE,{"derivedFrom":[makeQuery(id+"F5.opExtrude","SWEPT_FACE",FACE,{"disambiguationData":[OSD([sQuery(id+"F4.wireOp",EDGE,"E30")])]}),makeQuery(id+"F8.opExtrude","CAP_FACE",FACE,{"disambiguationData":[OSD([sQuery(id+"F7.wireOp",EDGE,"E67")])],"isStart":false})]});
            var Q2;
            Q2=makeQuery(id+"F8.boolean.opBoolean","INTERSECT",EDGE,{"disambiguationData":[OD(1.0)],"derivedFrom":[makeQuery(id+"F5.opExtrude","SWEPT_FACE",FACE,{"disambiguationData":[OSD([sQuery(id+"F4.wireOp",EDGE,"E30")])]}),makeQuery(id+"F8.opExtrude","SWEPT_FACE",FACE,{"disambiguationData":[OSD([sQuery(id+"F7.wireOp",EDGE,"E67")])]})]});
            var Q3;
            {var subQ0=sQuery(id+"F4.wireOp",EDGE,"E30");Q3=makeQuery(id+"F8.boolean.opBoolean","SPLIT",EDGE,{"disambiguationData":[TD([makeQuery(id+"F5.opExtrude","SWEPT_FACE",FACE,{"disambiguationData":[OSD([sQuery(id+"F4.wireOp",EDGE,"E35.filletArc")])]})])],"derivedFrom":makeQuery(id+"F5.opExtrude","CAP_EDGE",EDGE,{"disambiguationData":[OSD([subQ0])],"isStart":false})});}
            var Q4;
            {var subQ0=sQuery(id+"F0.wireOp",EDGE,"E25.7");var subQ1=sQuery(id+"F0.wireOp",EDGE,"E25.1");var subQ2=sQuery(id+"F0.wireOp",EDGE,"E25.6");var subQ3=sQuery(id+"F0.wireOp",EDGE,"E25.5");var subQ4=sQuery(id+"F0.wireOp",EDGE,"E25.4");var subQ5=sQuery(id+"F0.wireOp",EDGE,"E25.0");var subQ6=sQuery(id+"F0.wireOp",EDGE,"E25.2");var subQ7=sQuery(id+"F0.wireOp",EDGE,"E25.3");Q4=makeQuery(id+"F8.boolean.opBoolean","INTERSECT",EDGE,{"derivedFrom":[makeQuery(id+"F5.boolean.opBoolean","SPLIT",FACE,{"disambiguationData":[TD([makeQuery(id+"F2.opExtrude","SWEPT_FACE",FACE,{"disambiguationData":[OSD([subQ5])]})])],"derivedFrom":makeQuery(id+"F3.boolean.opBoolean","COPY",FACE,{"derivedFrom":makeQuery(id+"F3.opExtrude","CAP_FACE",FACE,{"disambiguationData":[OSD([subQ5,subQ1,subQ6,subQ7,subQ4,subQ3,subQ2,subQ0])],"isStart":false})})}),makeQuery(id+"F8.opExtrude","SWEPT_FACE",FACE,{"disambiguationData":[OSD([sQuery(id+"F7.wireOp",EDGE,"E67")])]})]});}
            var Q5;
            Q5=makeQuery(id+"F8.boolean.opBoolean","INTERSECT",EDGE,{"disambiguationData":[OD(0.0)],"derivedFrom":[makeQuery(id+"F5.opExtrude","SWEPT_FACE",FACE,{"disambiguationData":[OSD([sQuery(id+"F4.wireOp",EDGE,"E30")])]}),makeQuery(id+"F8.opExtrude","SWEPT_FACE",FACE,{"disambiguationData":[OSD([sQuery(id+"F7.wireOp",EDGE,"E67")])]})]});
            fillet(context, id + "F14", {"entities" : qUnion([Q0, Q1, Q2, Q3, Q4, Q5]), "radius" : 3 * mm, "tangentPropagation" : true, "allowEdgeOverflow" : false});
        }
        {
            var Q0;
            Q0=makeQuery(id+"F1.opExtrude","CAP_EDGE",EDGE,{"disambiguationData":[OSD([sQuery(id+"F0.wireOp",EDGE,"E1.bottom")])],"isStart":false});
            fillet(context, id + "F15", {"entities" : qUnion([Q0]), "radius" : 2 * mm, "tangentPropagation" : true, "allowEdgeOverflow" : false});
        }
        {
            var Q0;
            {var subQ0=sQuery(id+"F0.wireOp",EDGE,"E22.filletArc");var subQ1=sQuery(id+"F0.wireOp",EDGE,"E7");var subQ2=sQuery(id+"F0.wireOp",EDGE,"E6");var subQ3=sQuery(id+"F0.wireOp",EDGE,"E5");var subQ4=sQuery(id+"F0.wireOp",EDGE,"E4");var subQ5=sQuery(id+"F0.wireOp",EDGE,"E1.bottom");var subQ6=sQuery(id+"F0.wireOp",EDGE,"E21.filletArc");var subQ7=sQuery(id+"F0.wireOp",EDGE,"E1.top");var subQ8=sQuery(id+"F0.wireOp",EDGE,"E1.left");var subQ9=sQuery(id+"F0.wireOp",EDGE,"E1.right");var subQ10=sQuery(id+"F0.wireOp",EDGE,"E23.filletArc");var subQ11=sQuery(id+"F0.wireOp",EDGE,"E24.filletArc");Q0=makeQuery(id+"F2.boolean.opBoolean","SPLIT",FACE,{"disambiguationData":[TD([makeQuery(id+"F1.opExtrude","SWEPT_FACE",FACE,{"disambiguationData":[OSD([subQ5])]})])],"derivedFrom":makeQuery(id+"F1.opExtrude","CAP_FACE",FACE,{"disambiguationData":[OSD([subQ5,subQ7,subQ8,subQ9,subQ4,subQ3,subQ2,subQ1,subQ6,subQ0,subQ10,subQ11])],"isStart":true})});}
            var sketch = newSketch(context, id + "F16", { "sketchPlane" : qUnion([Q0])});
            skPoint(sketch, "E79.endSnap0", {"position": v(0.1, 63.2) * mm});
            skCircle(sketch, "E80", {"center": v(0.1, 104.25) * mm, "radius": 6 * mm});
            skLineSegment(sketch, "E81", {"start": v(-14.94, 104.25) * mm, "end": v(-14.94, 92.25) * mm});
            skLineSegment(sketch, "E82", {"start": v(-14.94, 92.25) * mm, "end": v(-32.94, 74.25) * mm});
            skLineSegment(sketch, "E83", {"start": v(15.06, 92.25) * mm, "end": v(15.06, 104.25) * mm});
            skLineSegment(sketch, "E84", {"start": v(15.06, 92.25) * mm, "end": v(33.06, 74.25) * mm});
            skArc(sketch, "E85", {"start": v(15.06, 104.25) * mm, "mid": v(0.06, 119.25) * mm, "end": v(-14.94, 104.25) * mm});
            skLineSegment(sketch, "E86", {"start": v(0.1, 104.25) * mm, "end": v(0.1, 74.25) * mm, "construction": true});
            skArc(sketch, "E87.MirrorCS", {"start": v(-14.86, 104.25) * mm, "mid": v(0.14, 119.25) * mm, "end": v(15.14, 104.25) * mm});
            skLineSegment(sketch, "E88.MirrorCS", {"start": v(15.14, 92.25) * mm, "end": v(33.14, 74.25) * mm});
            skLineSegment(sketch, "E89.MirrorCS", {"start": v(-14.86, 92.25) * mm, "end": v(-32.86, 74.25) * mm});
            skLineSegment(sketch, "E90.MirrorCS", {"start": v(15.14, 104.25) * mm, "end": v(15.14, 92.25) * mm});
            skLineSegment(sketch, "E91.MirrorCS", {"start": v(-14.86, 92.25) * mm, "end": v(-14.86, 104.25) * mm});
            skLineSegment(sketch, "E92", {"start": v(-74.25, 0) * mm, "end": v(74.25, 0) * mm});
            skLineSegment(sketch, "E93", {"start": v(-74.25, 0) * mm, "end": v(74.25, 0) * mm, "construction": true});
            skLineSegment(sketch, "E94.MirrorCS", {"start": v(15.06, -92.25) * mm, "end": v(15.06, -104.25) * mm});
            skLineSegment(sketch, "E95.MirrorCS", {"start": v(-14.86, -92.25) * mm, "end": v(-14.86, -104.25) * mm});
            skLineSegment(sketch, "E96.MirrorCS", {"start": v(15.14, -104.25) * mm, "end": v(15.14, -92.25) * mm});
            skLineSegment(sketch, "E97.MirrorCS", {"start": v(-14.94, -104.25) * mm, "end": v(-14.94, -92.25) * mm});
            skCircle(sketch, "E98.MirrorC", {"center": v(0.1, -104.25) * mm, "radius": 6 * mm});
            skLineSegment(sketch, "E99.MirrorCS", {"start": v(15.14, -92.25) * mm, "end": v(33.14, -74.25) * mm});
            skLineSegment(sketch, "E100.MirrorCS", {"start": v(-14.86, -92.25) * mm, "end": v(-32.86, -74.25) * mm});
            skLineSegment(sketch, "E101.MirrorCS", {"start": v(15.06, -92.25) * mm, "end": v(33.06, -74.25) * mm});
            skLineSegment(sketch, "E102.MirrorCS", {"start": v(-14.94, -92.25) * mm, "end": v(-32.94, -74.25) * mm});
            skArc(sketch, "E103.MirrorCS", {"start": v(-14.86, -104.25) * mm, "mid": v(0.14, -119.25) * mm, "end": v(15.14, -104.25) * mm});
            skArc(sketch, "E104.MirrorCS", {"start": v(15.06, -104.25) * mm, "mid": v(0.06, -119.25) * mm, "end": v(-14.94, -104.25) * mm});
            skPoint(sketch, "E105.MirrorP", {"position": v(0.1, -63.2) * mm});
            skLineSegment(sketch, "E106.MirrorCS", {"start": v(0.1, -104.25) * mm, "end": v(0.1, -74.25) * mm, "construction": true});
            skSolve(sketch);
        }
        {
            var Q0;
            {var subQ3=sQuery(id+"F16.wireOp",EDGE,"E89.MirrorCS");Q0=makeQuery(id+"F16.imprint","IMPRINT",FACE,{"disambiguationData":[TD([[makeQuery(id+"F16.imprint","IMPRINT",EDGE,{"derivedFrom":subQ3}),1.0]])]});}
            var Q1;
            Q1=makeQuery(id+"F16.imprint","IMPRINT",FACE,{"disambiguationData":[TD([[makeQuery(id+"F16.imprint","IMPRINT",EDGE,{"derivedFrom":makeQuery(id+"F1.opExtrude","CAP_EDGE",EDGE,{"disambiguationData":[OSD([sQuery(id+"F0.wireOp",EDGE,"E4")])],"isStart":true})}),-1.0]])]});
            var Q2;
            Q2=makeQuery(id+"F16.imprint","IMPRINT",FACE,{"disambiguationData":[TD([[makeQuery(id+"F16.imprint","IMPRINT",EDGE,{"derivedFrom":makeQuery(id+"F1.opExtrude","CAP_EDGE",EDGE,{"disambiguationData":[OSD([sQuery(id+"F0.wireOp",EDGE,"E6")])],"isStart":true})}),-1.0]])]});
            var Q3;
            {var subQ1=sQuery(id+"F16.wireOp",EDGE,"E95.MirrorCS");Q3=makeQuery(id+"F16.imprint","IMPRINT",FACE,{"disambiguationData":[TD([[makeQuery(id+"F16.imprint","IMPRINT",EDGE,{"derivedFrom":subQ1}),1.0]])]});}
            var Q4;
            Q4=makeQuery(id+"F2.opExtrude","CAP_FACE",FACE,{"disambiguationData":[OSD([sQuery(id+"F0.wireOp",EDGE,"E12"),sQuery(id+"F0.wireOp",EDGE,"E13"),sQuery(id+"F0.wireOp",EDGE,"E14"),sQuery(id+"F0.wireOp",EDGE,"E15"),sQuery(id+"F0.wireOp",EDGE,"E17.filletArc"),sQuery(id+"F0.wireOp",EDGE,"E18.filletArc"),sQuery(id+"F0.wireOp",EDGE,"E19.filletArc"),sQuery(id+"F0.wireOp",EDGE,"E20.filletArc"),sQuery(id+"F0.wireOp",EDGE,"E25.0"),sQuery(id+"F0.wireOp",EDGE,"E25.1"),sQuery(id+"F0.wireOp",EDGE,"E25.2"),sQuery(id+"F0.wireOp",EDGE,"E25.3"),sQuery(id+"F0.wireOp",EDGE,"E25.4"),sQuery(id+"F0.wireOp",EDGE,"E25.5"),sQuery(id+"F0.wireOp",EDGE,"E25.6"),sQuery(id+"F0.wireOp",EDGE,"E25.7")])],"isStart":false});
            extrude(context, id + "F17", {"entities" : qUnion([Q0, Q1, Q2, Q3]), "operationType" : NewBodyOperationType.ADD, "endBound" : BoundingType.UP_TO_SURFACE, "endBoundEntityFace" : qUnion([Q4]), "depth" : 25 * mm});
        }
    });
